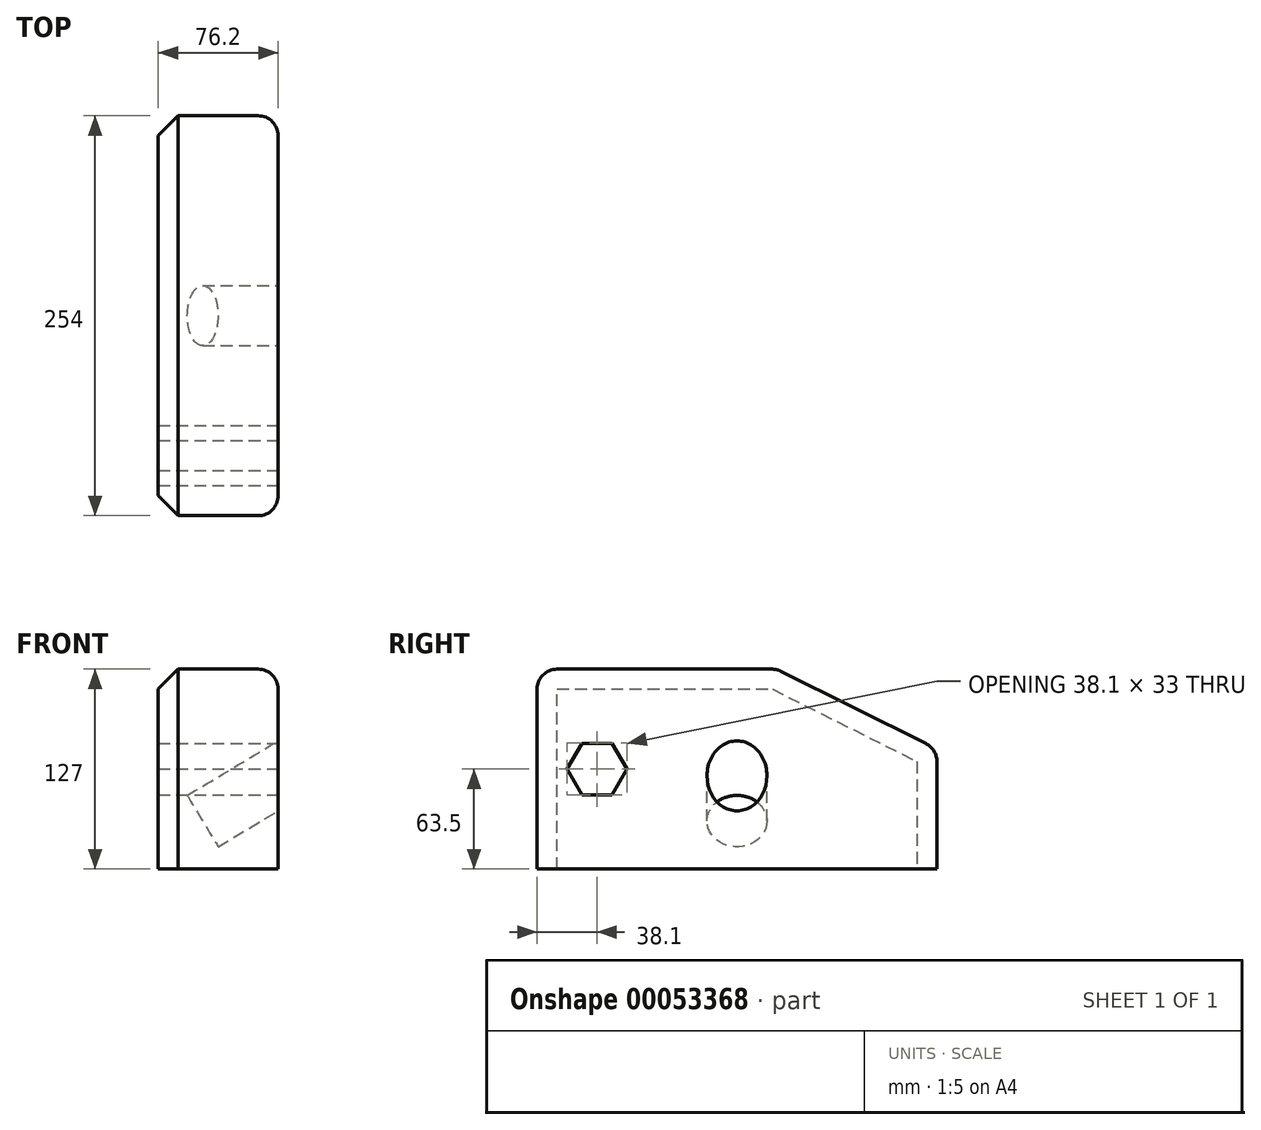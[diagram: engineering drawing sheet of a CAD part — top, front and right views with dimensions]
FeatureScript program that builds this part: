
annotation { "Feature Type Name" : "Feature", "Feature Type Description" : "" }
export const myFeature = defineFeature(function(context is Context, id is Id, definition is map)
    precondition{}
    {
        {
            var Q0;
            Q0=qCreatedBy(makeId("Front.planeOp"),FACE);
            var sketch = newSketch(context, id + "F0", { "sketchPlane" : qUnion([Q0])});
            skLineSegment(sketch, "E0.rect.bottom", {"start": v(38.1, 63.5) * mm, "end": v(-38.1, 63.5) * mm});
            skLineSegment(sketch, "E0.rect.top", {"start": v(38.1, -63.5) * mm, "end": v(-38.1, -63.5) * mm});
            skLineSegment(sketch, "E0.rect.left", {"start": v(38.1, 63.5) * mm, "end": v(38.1, -63.5) * mm});
            skLineSegment(sketch, "E0.rect.right", {"start": v(-38.1, 63.5) * mm, "end": v(-38.1, -63.5) * mm});
            skPoint(sketch, "E0.rect.middle", {"position": v(0, 0) * mm});
            skSolve(sketch);
        }
        {
            var Q0;
            Q0=makeQuery(id+"F0.imprint","IMPRINT",FACE,{"disambiguationData":[TD([[makeQuery(id+"F0.imprint","IMPRINT",EDGE,{"derivedFrom":sQuery(id+"F0.wireOp",EDGE,"E0.rect.bottom")}),1.0]])]});
            extrude(context, id + "F1", {"entities" : qUnion([Q0]), "endBound" : BoundingType.SYMMETRIC, "depth" : 254 * mm});
        }
        {
            var Q0;
            Q0=makeQuery(id+"F1.opExtrude","SWEPT_FACE",FACE,{"disambiguationData":[OSD([sQuery(id+"F0.wireOp",EDGE,"E0.rect.left")])]});
            var sketch = newSketch(context, id + "F2", { "sketchPlane" : qUnion([Q0])});
            skCircle(sketch, "E1.cCircle", {"center": v(-88.9, 0) * mm, "radius": 19.05 * mm, "construction": true});
            skLineSegment(sketch, "E1.0", {"start": v(-79.38, 16.5) * mm, "end": v(-69.85, 0) * mm});
            skLineSegment(sketch, "E1.1", {"start": v(-69.85, 0) * mm, "end": v(-79.38, -16.5) * mm});
            skLineSegment(sketch, "E1.2", {"start": v(-79.38, -16.5) * mm, "end": v(-98.42, -16.5) * mm});
            skLineSegment(sketch, "E1.3", {"start": v(-98.43, -16.5) * mm, "end": v(-107.95, 0) * mm});
            skLineSegment(sketch, "E1.4", {"start": v(-107.95, 0) * mm, "end": v(-98.42, 16.5) * mm});
            skLineSegment(sketch, "E1.5", {"start": v(-98.43, 16.5) * mm, "end": v(-79.38, 16.5) * mm});
            skSolve(sketch);
        }
        {
            var Q0;
            Q0 = qSketchRegion(id + "F2", true);
            extrude(context, id + "F3", {"entities" : qUnion([Q0]), "operationType" : NewBodyOperationType.REMOVE, "endBound" : BoundingType.THROUGH_ALL, "oppositeDirection" : true, "depth" : 25.4 * mm});
        }
        {
            var Q0;
            Q0=qCreatedBy(makeId("Right.planeOp"),FACE);
            var sketch = newSketch(context, id + "F8", { "sketchPlane" : qUnion([Q0])});
            skLineSegment(sketch, "E2", {"start": v(-101.6, 127) * mm, "end": v(152.4, 0) * mm});
            skSolve(sketch);
        }
        {
            var Q0;
            Q0 = qBodyType(qCreatedBy(id + "F8" ,EDGE), BodyType.WIRE);
            extrude(context, id + "F9", {"bodyType" : ToolBodyType.SURFACE, "surfaceEntities" : qUnion([Q0]), "endBound" : BoundingType.SYMMETRIC, "depth" : 254 * mm});
        }
        {
            var Q0;
            Q0=makeQuery(id+"F9.opExtrude","SWEPT_FACE",FACE,{"disambiguationData":[OSD([sQuery(id+"F8.wireOp",EDGE,"E2")])]});
            extrude(context, id + "F10", {"entities" : qUnion([Q0]), "operationType" : NewBodyOperationType.REMOVE, "endBound" : BoundingType.THROUGH_ALL, "oppositeDirection" : true, "depth" : 25.4 * mm});
        }
        {
            var Q0;
            Q0=makeQuery(id+"F1.opExtrude","CAP_VERTEX",VERTEX,{"disambiguationData":[OSD([sQuery(id+"F0.wireOp",EDGE,"E0.rect.top"),sQuery(id+"F0.wireOp",EDGE,"E0.rect.left")])],"isStart":false});
            var Q1;
            Q1=makeQuery(id+"F1.opExtrude","CAP_VERTEX",VERTEX,{"disambiguationData":[OSD([sQuery(id+"F0.wireOp",EDGE,"E0.rect.top"),sQuery(id+"F0.wireOp",EDGE,"E0.rect.left")])],"isStart":true});
            var Q2;
            Q2=makeQuery(id+"F1.opExtrude","CAP_VERTEX",VERTEX,{"disambiguationData":[OSD([sQuery(id+"F0.wireOp",EDGE,"E0.rect.bottom"),sQuery(id+"F0.wireOp",EDGE,"E0.rect.right")])],"isStart":false});
            cPlane(context, id + "F4", {"entities" : qUnion([Q0, Q1, Q2]), "cplaneType" : CPlaneType.THREE_POINT, "offset" : 152.4 * mm, "width" : 152.4 * mm, "height" : 152.4 * mm});
        }
        {
            var Q0;
            Q0=qCreatedBy(id+"F4.planeOp",FACE);
            var sketch = newSketch(context, id + "F5", { "sketchPlane" : qUnion([Q0])});
            skCircle(sketch, "E3", {"center": v(0, -23.25) * mm, "radius": 19.05 * mm});
            skSolve(sketch);
        }
        {
            var Q0;
            Q0 = qSketchRegion(id + "F5", true);
            extrude(context, id + "F6", {"entities" : qUnion([Q0]), "operationType" : NewBodyOperationType.REMOVE, "depth" : 25.4 * mm, "hasSecondDirection" : true, "secondDirectionBound" : SecondDirectionBoundingType.THROUGH_ALL, "secondDirectionOppositeDirection" : true, "secondDirectionDepth" : 25.4 * mm});
        }
        {
            var Q0;
            Q0=makeQuery(id+"F1.opExtrude","SWEPT_EDGE",EDGE,{"disambiguationData":[OSD([sQuery(id+"F0.wireOp",EDGE,"E0.rect.bottom"),sQuery(id+"F0.wireOp",EDGE,"E0.rect.left")])]});
            var Q1;
            Q1=makeQuery(id+"F1.opExtrude","CAP_EDGE",EDGE,{"disambiguationData":[OSD([sQuery(id+"F0.wireOp",EDGE,"E0.rect.bottom")])],"isStart":false});
            var Q2;
            Q2=makeQuery(id+"F1.opExtrude","CAP_EDGE",EDGE,{"disambiguationData":[OSD([sQuery(id+"F0.wireOp",EDGE,"E0.rect.left")])],"isStart":false});
            var Q3;
            Q3=makeQuery(id+"F10.boolean.opBoolean","INTERSECT",EDGE,{"derivedFrom":[makeQuery(id+"F1.opExtrude","SWEPT_FACE",FACE,{"disambiguationData":[OSD([sQuery(id+"F0.wireOp",EDGE,"E0.rect.left")])]}),makeQuery(id+"F10.opExtrude","CAP_FACE",FACE,{"disambiguationData":[OSD([sQuery(id+"F8.wireOp",EDGE,"E2")])],"isStart":true})]});
            var Q4;
            Q4=makeQuery(id+"F1.opExtrude","CAP_EDGE",EDGE,{"disambiguationData":[OSD([sQuery(id+"F0.wireOp",EDGE,"E0.rect.left")])],"isStart":true});
            var Q5;
            Q5=makeQuery(id+"F10.boolean.opBoolean","INTERSECT",EDGE,{"derivedFrom":[makeQuery(id+"F1.opExtrude","CAP_FACE",FACE,{"disambiguationData":[OSD([sQuery(id+"F0.wireOp",EDGE,"E0.rect.bottom"),sQuery(id+"F0.wireOp",EDGE,"E0.rect.top"),sQuery(id+"F0.wireOp",EDGE,"E0.rect.left"),sQuery(id+"F0.wireOp",EDGE,"E0.rect.right")])],"isStart":true}),makeQuery(id+"F10.opExtrude","CAP_FACE",FACE,{"disambiguationData":[OSD([sQuery(id+"F8.wireOp",EDGE,"E2")])],"isStart":true})]});
            var Q6;
            Q6=makeQuery(id+"F10.boolean.opBoolean","INTERSECT",EDGE,{"derivedFrom":[makeQuery(id+"F1.opExtrude","SWEPT_FACE",FACE,{"disambiguationData":[OSD([sQuery(id+"F0.wireOp",EDGE,"E0.rect.bottom")])]}),makeQuery(id+"F10.opExtrude","CAP_FACE",FACE,{"disambiguationData":[OSD([sQuery(id+"F8.wireOp",EDGE,"E2")])],"isStart":true})]});
            fillet(context, id + "F7", {"entities" : qUnion([Q0, Q1, Q2, Q3, Q4, Q5, Q6]), "radius" : 12.7 * mm, "tangentPropagation" : true, "allowEdgeOverflow" : false});
        }
        {
            var Q0;
            Q0=makeQuery(id+"F1.opExtrude","CAP_EDGE",EDGE,{"disambiguationData":[OSD([sQuery(id+"F0.wireOp",EDGE,"E0.rect.right")])],"isStart":false});
            chamfer(context, id + "F11", {"entities" : qUnion([Q0]), "width" : 12.7 * mm, "tangentPropagation" : true});
        }
    });
